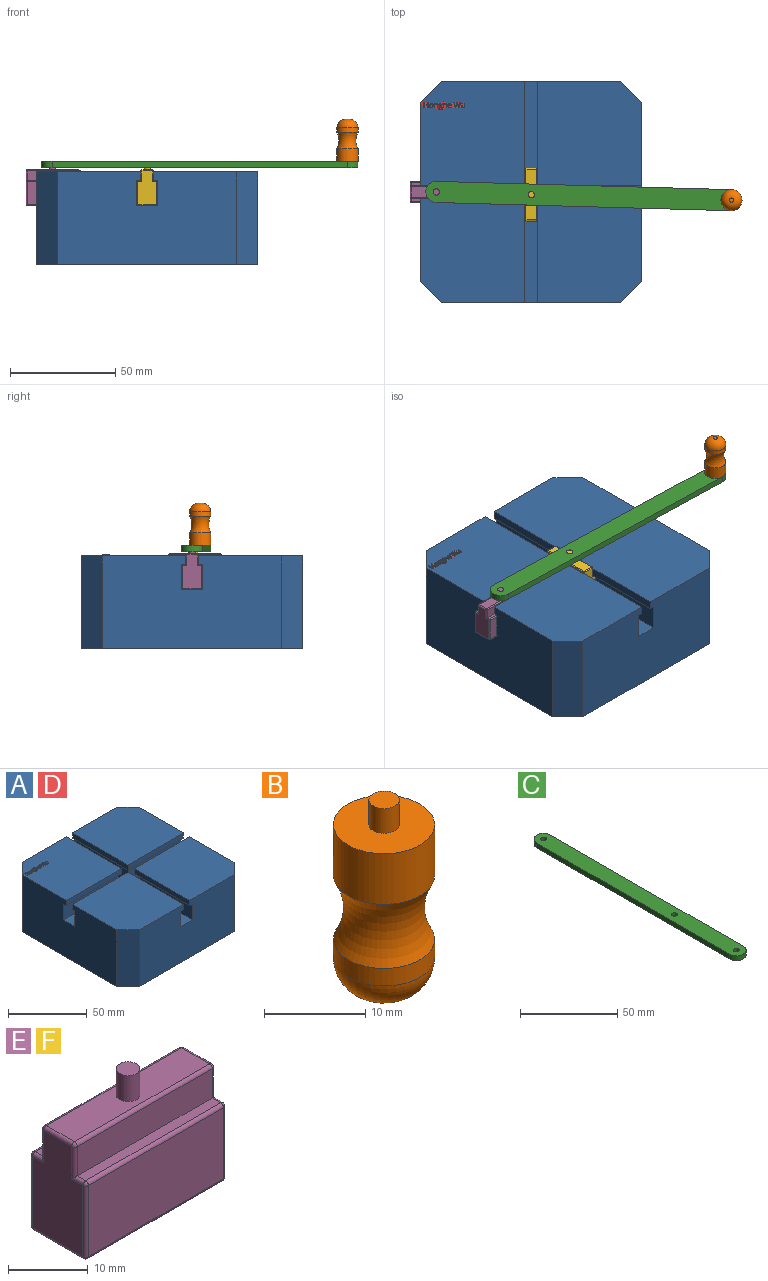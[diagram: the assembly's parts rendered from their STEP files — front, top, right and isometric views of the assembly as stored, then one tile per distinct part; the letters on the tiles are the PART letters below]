
ASSEMBLY  parts=6 mates=5
PART A: 210 faces, bbox 105x105x44.5 mm
  f0: plane 49.5x49.5mm, normal (0,0,1), area 2382.3mm2, adj f10,f15,f16,f19,f33,f34,f35,f36
  f1: plane 49.5x49.5mm, normal (0,0,1), area 2400.2mm2, adj f10,f11,f12,f25,f28
  f2: plane 49.5x49.5mm, normal (0,0,-1), area 194mm2, adj f10,f15,f19,f21,f31,f33
  f3: plane 49.5x49.5mm, normal (0,0,-1), area 194mm2, adj f10,f12,f23,f25,f27,f28
  f4: plane 49.5x4mm, normal (0,-1,0), area 198mm2, adj f9,f17,f20,f32
  f5: plane 47.5x12mm, normal (0,-1,0), area 570mm2, adj f9,f20,f22,f30
  f6: plane 47.5x12mm, normal (0,1,0), area 570mm2, adj f9,f22,f24,f29
  f7: plane 49.5x4mm, normal (0,1,0), area 198mm2, adj f8,f9,f24,f26
  f8: plane 49.5x49.5mm, normal (0,0,1), area 2400.2mm2, adj f7,f9,f12,f13,f26
  f9: plane 85x44mm, normal (1,0,0), area 3596mm2, adj f4,f5,f6,f7,f8,f13,f14,f17
  f10: plane 85x44mm, normal (-1,0,0), area 3596mm2, adj f0,f1,f2,f3,f11,f16,f18,f19
  f11: plane 44x10mm, normal (-0.71,-0.71,0), area 622.3mm2, adj f1,f10,f12,f18
  f12: plane 85x44mm, normal (0,-1,0), area 3596mm2, adj f1,f3,f8,f11,f13,f18,f22,f24
  f13: plane 44x10mm, normal (0.71,-0.71,0), area 622.3mm2, adj f8,f9,f12,f18
  f14: plane 44x10mm, normal (0.71,0.71,0), area 622.3mm2, adj f9,f15,f17,f18
  f15: plane 85x44mm, normal (0,1,0), area 3596mm2, adj f0,f2,f14,f16,f17,f18,f20,f22
  f16: plane 44x10mm, normal (-0.71,0.71,0), area 622.3mm2, adj f0,f10,f15,f18
  f17: plane 49.5x49.5mm, normal (0,0,1), area 2400.2mm2, adj f4,f9,f14,f15,f32
  f18: plane 105x105mm, normal (0,0,-1), area 10825mm2, adj f9,f10,f11,f12,f13,f14,f15,f16
  f19: plane 49.5x4mm, normal (0,-1,0), area 198mm2, adj f0,f2,f10,f33
  f20: plane 49.5x49.5mm, normal (0,0,-1), area 194mm2, adj f4,f5,f9,f15,f30,f32
  f21: plane 47.5x12mm, normal (0,-1,0), area 570mm2, adj f2,f10,f22,f31
  f22: plane 105x105mm, normal (0,0,1), area 2000mm2, adj f5,f6,f9,f10,f12,f15,f21,f23
  f23: plane 47.5x12mm, normal (0,1,0), area 570mm2, adj f3,f10,f22,f27
  f24: plane 49.5x49.5mm, normal (0,0,-1), area 194mm2, adj f6,f7,f9,f12,f26,f29
  f25: plane 49.5x4mm, normal (0,1,0), area 198mm2, adj f1,f3,f10,f28
  f26: plane 49.5x4mm, normal (-1,0,0), area 198mm2, adj f7,f8,f12,f24
  f27: plane 47.5x12mm, normal (1,0,0), area 570mm2, adj f3,f12,f22,f23
  f28: plane 49.5x4mm, normal (1,0,0), area 198mm2, adj f1,f3,f12,f25
  f29: plane 47.5x12mm, normal (-1,0,0), area 570mm2, adj f6,f12,f22,f24
  f30: plane 47.5x12mm, normal (-1,0,0), area 570mm2, adj f5,f15,f20,f22
  f31: plane 47.5x12mm, normal (1,0,0), area 570mm2, adj f2,f15,f21,f22
  f32: plane 49.5x4mm, normal (-1,0,0), area 198mm2, adj f4,f15,f17,f20
  f33: plane 49.5x4mm, normal (1,0,0), area 198mm2, adj f0,f2,f15,f19
  f34: plane 0.5x0.3mm, normal (0,-1,0), area 0.2mm2, adj f0,f35,f45,f46
  f35: plane 2.62x0.5mm, normal (1,0,0), area 1.3mm2, adj f0,f34,f36,f46
  f36: plane 0.5x0.3mm, normal (0,1,0), area 0.2mm2, adj f0,f35,f37,f46
  f37: plane 1.11x0.5mm, normal (-1,0,0), area 0.6mm2, adj f0,f36,f38,f46
  f38: plane 1.38x0.5mm, normal (0,1,0), area 0.7mm2, adj f0,f37,f39,f46
  f39: plane 1.11x0.5mm, normal (1,0,0), area 0.6mm2, adj f0,f38,f40,f46
  f40: plane 0.5x0.3mm, normal (0,1,0), area 0.2mm2, adj f0,f39,f41,f46
  f41: plane 2.62x0.5mm, normal (-1,0,0), area 1.3mm2, adj f0,f40,f42,f46
  f42: plane 0.5x0.3mm, normal (0,-1,0), area 0.2mm2, adj f0,f41,f43,f46
  f43: plane 1.23x0.5mm, normal (1,0,0), area 0.6mm2, adj f0,f42,f44,f46
  f44: plane 1.38x0.5mm, normal (0,-1,0), area 0.7mm2, adj f0,f43,f45,f46
  f45: plane 1.23x0.5mm, normal (-1,0,0), area 0.6mm2, adj f0,f34,f44,f46
  f46: plane 2.62x1.99mm, normal (0,0,1), area 2mm2, adj f34,f35,f36,f37,f38,f39,f40,f41
  f47: extruded ~0.57x0.5mm, area 0.3mm2, adj f48,f63,f64,f65
  f48: extruded ~0.57x0.5mm, area 0.3mm2, adj f47,f49,f64,f65
  f49: extruded ~0.5x0.44mm, area 0.2mm2, adj f48,f50,f64,f65
  f50: extruded ~0.5x0.45mm, area 0.3mm2, adj f49,f51,f64,f65
  f51: extruded ~0.57x0.5mm, area 0.3mm2, adj f50,f52,f64,f65
  f52: extruded ~0.57x0.5mm, area 0.3mm2, adj f51,f53,f64,f65
  f53: extruded ~0.5x0.44mm, area 0.3mm2, adj f52,f63,f64,f65
  f54: extruded ~0.75x0.5mm, area 0.4mm2, adj f0,f55,f62,f64
  f55: extruded ~0.74x0.5mm, area 0.4mm2, adj f0,f54,f56,f64
  f56: extruded ~0.65x0.5mm, area 0.4mm2, adj f0,f55,f57,f64
  f57: extruded ~0.67x0.5mm, area 0.4mm2, adj f0,f56,f58,f64
  f58: extruded ~0.75x0.5mm, area 0.4mm2, adj f0,f57,f59,f64
  f59: extruded ~0.54x0.5mm, area 0.3mm2, adj f0,f58,f60,f64
  f60: extruded ~0.5x0.35mm, area 0.2mm2, adj f0,f59,f61,f64
  f61: extruded ~0.5x0.47mm, area 0.2mm2, adj f0,f60,f62,f64
  f62: extruded ~0.67x0.5mm, area 0.4mm2, adj f0,f54,f61,f64
  f63: extruded ~0.5x0.44mm, area 0.3mm2, adj f47,f53,f64,f65
  f64: plane 2.03x1.8mm, normal (0,0,1), area 1.5mm2, adj f47,f48,f49,f50,f51,f52,f53,f54
  f65: plane 1.53x1.19mm, normal (0,0,1), area 1.5mm2, adj f47,f48,f49,f50,f51,f52,f53,f63
  f66: plane 1.27x0.5mm, normal (-1,0,0), area 0.6mm2, adj f0,f67,f82,f83
  f67: plane 0.5x0.3mm, normal (0,-1,0), area 0.1mm2, adj f0,f66,f68,f83
  f68: plane 1.28x0.5mm, normal (1,0,0), area 0.6mm2, adj f0,f67,f69,f83
  f69: extruded ~0.55x0.5mm, area 0.3mm2, adj f0,f68,f70,f83
  f70: extruded ~0.53x0.5mm, area 0.3mm2, adj f0,f69,f71,f83
  f71: extruded ~0.5x0.37mm, area 0.2mm2, adj f0,f70,f72,f83
  f72: extruded ~0.5x0.26mm, area 0.2mm2, adj f0,f71,f73,f83
  f73: plane 0.5x0.01mm, normal (0,1,0), area 0mm2, adj f0,f72,f74,f83
  f74: plane 0.5x0.27mm, normal (0.98,0.18,0), area 0.1mm2, adj f0,f73,f75,f83
  f75: plane 0.5x0.24mm, normal (0,1,0), area 0.1mm2, adj f0,f74,f76,f83
  f76: plane 1.96x0.5mm, normal (-1,0,0), area 1mm2, adj f0,f75,f77,f83
  f77: plane 0.5x0.3mm, normal (0,-1,0), area 0.1mm2, adj f0,f76,f78,f83
  f78: plane 1.03x0.5mm, normal (1,0,0), area 0.5mm2, adj f0,f77,f79,f83
  f79: extruded ~0.55x0.5mm, area 0.3mm2, adj f0,f78,f80,f83
  f80: extruded ~0.5x0.45mm, area 0.2mm2, adj f0,f79,f81,f83
  f81: extruded ~0.5x0.34mm, area 0.2mm2, adj f0,f80,f82,f83
  f82: extruded ~0.5x0.36mm, area 0.2mm2, adj f0,f66,f81,f83
  f83: plane 2x1.64mm, normal (0,0,1), area 1.4mm2, adj f66,f67,f68,f69,f70,f71,f72,f73
  f84: extruded ~0.5x0.31mm, area 0.2mm2, adj f85,f127,f128,f129
  f85: extruded ~0.5x0.33mm, area 0.2mm2, adj f84,f86,f128,f129
  f86: extruded ~0.5x0.32mm, area 0.2mm2, adj f85,f87,f128,f129
  f87: extruded ~0.5x0.44mm, area 0.4mm2, adj f86,f88,f128,f129
  f88: extruded ~0.5x0.43mm, area 0.3mm2, adj f87,f127,f128,f129
  f89: extruded ~0.5x0.24mm, area 0.1mm2, adj f90,f125,f128,f130
  f90: extruded ~0.5x0.28mm, area 0.2mm2, adj f89,f91,f128,f130
  f91: extruded ~0.5x0.32mm, area 0.2mm2, adj f90,f92,f128,f130
  f92: plane 0.5x0.36mm, normal (0,-1,0), area 0.2mm2, adj f91,f93,f128,f130
  f93: extruded ~0.5x0.37mm, area 0.2mm2, adj f92,f94,f128,f130
  f94: extruded ~0.5x0.22mm, area 0.1mm2, adj f93,f95,f128,f130
  f95: extruded ~0.5x0.3mm, area 0.2mm2, adj f94,f96,f128,f130
  f96: extruded ~0.55x0.5mm, area 0.3mm2, adj f95,f125,f128,f130
  f97: plane 0.5x0.19mm, normal (1,0,0), area 0.1mm2, adj f0,f98,f126,f128
  f98: plane 0.68x0.5mm, normal (0,1,0), area 0.3mm2, adj f0,f97,f99,f128
  f99: extruded ~0.5x0.28mm, area 0.1mm2, adj f0,f98,f100,f128
  f100: extruded ~0.55x0.5mm, area 0.3mm2, adj f0,f99,f101,f128
  f101: extruded ~0.5x0.5mm, area 0.3mm2, adj f0,f100,f102,f128
  f102: extruded ~0.5x0.34mm, area 0.2mm2, adj f0,f101,f103,f128
  f103: extruded ~0.5x0.25mm, area 0.2mm2, adj f0,f102,f104,f128
  f104: extruded ~0.5x0.18mm, area 0.1mm2, adj f0,f103,f105,f128
  f105: extruded ~0.5x0.19mm, area 0.1mm2, adj f0,f104,f106,f128
  f106: extruded ~0.5x0.17mm, area 0.1mm2, adj f0,f105,f107,f128
  f107: extruded ~0.5x0.13mm, area 0.1mm2, adj f0,f106,f108,f128
  f108: extruded ~0.5x0.32mm, area 0.2mm2, adj f0,f107,f109,f128
  f109: extruded ~0.5x0.31mm, area 0.2mm2, adj f0,f108,f110,f128
  f110: extruded ~0.5x0.41mm, area 0.2mm2, adj f0,f109,f111,f128
  f111: extruded ~0.59x0.5mm, area 0.3mm2, adj f0,f110,f112,f128
  f112: extruded ~0.76x0.5mm, area 0.4mm2, adj f0,f111,f113,f128
  f113: extruded ~0.5x0.5mm, area 0.3mm2, adj f0,f112,f114,f128
  f114: extruded ~0.5x0.39mm, area 0.2mm2, adj f0,f113,f115,f128
  f115: extruded ~0.5x0.49mm, area 0.3mm2, adj f0,f114,f116,f128
  f116: plane 0.5x0.35mm, normal (0,1,0), area 0.2mm2, adj f0,f115,f117,f128
  f117: extruded ~0.5x0.23mm, area 0.1mm2, adj f0,f116,f118,f128
  f118: extruded ~0.5x0.12mm, area 0.1mm2, adj f0,f117,f119,f128
  f119: extruded ~0.5x0.25mm, area 0.2mm2, adj f0,f118,f120,f128
  f120: extruded ~0.5x0.16mm, area 0.1mm2, adj f0,f119,f121,f128
  f121: extruded ~0.54x0.5mm, area 0.3mm2, adj f0,f120,f122,f128
  f122: extruded ~0.5x0.46mm, area 0.3mm2, adj f0,f121,f123,f128
  f123: extruded ~0.5x0.23mm, area 0.1mm2, adj f0,f122,f124,f128
  f124: extruded ~0.5x0.16mm, area 0.1mm2, adj f0,f123,f126,f128
  f125: extruded ~0.5x0.38mm, area 0.2mm2, adj f89,f96,f128,f130
  f126: plane 0.5x0.36mm, normal (0.12,-0.99,0), area 0.2mm2, adj f0,f97,f124,f128
  f127: extruded ~0.5x0.32mm, area 0.2mm2, adj f84,f88,f128,f129
  f128: plane 2.88x1.85mm, normal (0,0,1), area 2.2mm2, adj f84,f85,f86,f87,f88,f89,f90,f91
  f129: plane 0.88x0.86mm, normal (0,0,1), area 0.6mm2, adj f84,f85,f86,f87,f88,f127
  f130: plane 1.25x0.7mm, normal (0,0,1), area 0.7mm2, adj f89,f90,f91,f92,f93,f94,f95,f96
  f131: plane 1.27x0.5mm, normal (-1,0,0), area 0.6mm2, adj f0,f132,f148,f149
  f132: plane 0.5x0.3mm, normal (0,-1,0), area 0.1mm2, adj f0,f131,f133,f149
  f133: plane 1.28x0.5mm, normal (1,0,0), area 0.6mm2, adj f0,f132,f134,f149
  f134: extruded ~0.54x0.5mm, area 0.3mm2, adj f0,f133,f135,f149
  f135: extruded ~0.54x0.5mm, area 0.3mm2, adj f0,f134,f136,f149
  f136: extruded ~0.5x0.37mm, area 0.2mm2, adj f0,f135,f137,f149
  f137: extruded ~0.5x0.25mm, area 0.2mm2, adj f0,f136,f138,f149
  f138: plane 0.5x0.02mm, normal (0,1,0), area 0mm2, adj f0,f137,f139,f149
  f139: extruded ~0.5x0.25mm, area 0.1mm2, adj f0,f138,f140,f149
  f140: plane 0.84x0.5mm, normal (1,0,0), area 0.4mm2, adj f0,f139,f141,f149
  f141: plane 0.5x0.3mm, normal (0,1,0), area 0.1mm2, adj f0,f140,f142,f149
  f142: plane 2.79x0.5mm, normal (-1,0,0), area 1.4mm2, adj f0,f141,f143,f149
  f143: plane 0.5x0.3mm, normal (0,-1,0), area 0.1mm2, adj f0,f142,f144,f149
  f144: plane 1.03x0.5mm, normal (1,0,0), area 0.5mm2, adj f0,f143,f145,f149
  f145: extruded ~0.55x0.5mm, area 0.3mm2, adj f0,f144,f146,f149
  f146: extruded ~0.5x0.45mm, area 0.2mm2, adj f0,f145,f147,f149
  f147: extruded ~0.5x0.34mm, area 0.2mm2, adj f0,f146,f148,f149
  f148: extruded ~0.5x0.36mm, area 0.2mm2, adj f0,f131,f147,f149
  f149: plane 2.79x1.64mm, normal (0,0,1), area 1.6mm2, adj f131,f132,f133,f134,f135,f136,f137,f138
  f150: extruded ~0.5x0.38mm, area 0.2mm2, adj f151,f168,f169,f170
  f151: extruded ~0.5x0.36mm, area 0.2mm2, adj f150,f152,f169,f170
  f152: extruded ~0.5x0.43mm, area 0.2mm2, adj f151,f153,f169,f170
  f153: plane 1.03x0.5mm, normal (0,1,0), area 0.5mm2, adj f152,f168,f169,f170
  f154: extruded ~0.69x0.5mm, area 0.4mm2, adj f0,f155,f167,f169
  f155: extruded ~0.5x0.34mm, area 0.2mm2, adj f0,f154,f156,f169
  f156: extruded ~0.5x0.3mm, area 0.2mm2, adj f0,f155,f157,f169
  f157: plane 0.5x0.27mm, normal (1,0,0), area 0.1mm2, adj f0,f156,f158,f169
  f158: extruded ~0.63x0.5mm, area 0.3mm2, adj f0,f157,f159,f169
  f159: extruded ~0.5x0.47mm, area 0.3mm2, adj f0,f158,f160,f169
  f160: extruded ~0.52x0.5mm, area 0.3mm2, adj f0,f159,f161,f169
  f161: plane 1.35x0.5mm, normal (0,-1,0), area 0.7mm2, adj f0,f160,f162,f169
  f162: plane 0.5x0.19mm, normal (1,0,0), area 0.1mm2, adj f0,f161,f163,f169
  f163: extruded ~0.64x0.5mm, area 0.3mm2, adj f0,f162,f164,f169
  f164: extruded ~0.58x0.5mm, area 0.3mm2, adj f0,f163,f165,f169
  f165: extruded ~0.63x0.5mm, area 0.4mm2, adj f0,f164,f166,f169
  f166: extruded ~0.75x0.5mm, area 0.4mm2, adj f0,f165,f167,f169
  f167: extruded ~0.74x0.5mm, area 0.4mm2, adj f0,f154,f166,f169
  f168: extruded ~0.5x0.43mm, area 0.2mm2, adj f150,f153,f169,f170
  f169: plane 2.03x1.66mm, normal (0,0,1), area 1.5mm2, adj f150,f151,f152,f153,f154,f155,f156,f157
  f170: plane 1.03x0.58mm, normal (0,0,1), area 0.5mm2, adj f150,f151,f152,f153,f168
  f171: plane 0.5x0.3mm, normal (0,-1,0), area 0.2mm2, adj f0,f172,f190,f191
  f172: plane 2.62x0.7mm, normal (0.97,-0.26,0), area 1.4mm2, adj f0,f171,f173,f191
  f173: plane 0.5x0.32mm, normal (0,1,0), area 0.2mm2, adj f0,f172,f174,f191
  f174: plane 1.61x0.5mm, normal (-0.97,0.25,0), area 0.8mm2, adj f0,f173,f175,f191
  f175: extruded ~0.62x0.5mm, area 0.3mm2, adj f0,f174,f176,f191
  f176: extruded ~0.63x0.5mm, area 0.3mm2, adj f0,f175,f177,f191
  f177: plane 1.61x0.5mm, normal (0.96,0.29,0), area 0.8mm2, adj f0,f176,f178,f191
  f178: plane 0.5x0.32mm, normal (0,1,0), area 0.2mm2, adj f0,f177,f179,f191
  f179: plane 1.59x0.5mm, normal (-0.96,0.28,0), area 0.8mm2, adj f0,f178,f180,f191
  f180: extruded ~0.64x0.5mm, area 0.3mm2, adj f0,f179,f181,f191
  f181: extruded ~0.62x0.5mm, area 0.3mm2, adj f0,f180,f182,f191
  f182: plane 1.62x0.5mm, normal (0.97,0.25,0), area 0.8mm2, adj f0,f181,f183,f191
  f183: plane 0.5x0.32mm, normal (0,1,0), area 0.2mm2, adj f0,f182,f184,f191
  f184: plane 2.62x0.7mm, normal (-0.97,-0.26,0), area 1.4mm2, adj f0,f183,f185,f191
  f185: plane 0.5x0.3mm, normal (0,-1,0), area 0.2mm2, adj f0,f184,f186,f191
  f186: plane 1.74x0.51mm, normal (0.96,-0.28,0), area 0.9mm2, adj f0,f185,f187,f191
  f187: extruded ~0.52x0.5mm, area 0.3mm2, adj f0,f186,f188,f191
  f188: extruded ~0.5x0.21mm, area 0.1mm2, adj f0,f187,f189,f191
  f189: extruded ~0.5x0.29mm, area 0.2mm2, adj f0,f188,f190,f191
  f190: plane 1.75x0.53mm, normal (-0.96,-0.29,0), area 0.9mm2, adj f0,f171,f189,f191
  f191: plane 3.3x2.62mm, normal (0,0,1), area 2.9mm2, adj f171,f172,f173,f174,f175,f176,f177,f178
  f192: plane 1.27x0.5mm, normal (1,0,0), area 0.6mm2, adj f0,f193,f208,f209
  f193: plane 0.5x0.3mm, normal (0,1,0), area 0.2mm2, adj f0,f192,f194,f209
  f194: plane 1.28x0.5mm, normal (-1,0,0), area 0.6mm2, adj f0,f193,f195,f209
  f195: extruded ~0.54x0.5mm, area 0.3mm2, adj f0,f194,f196,f209
  f196: extruded ~0.54x0.5mm, area 0.3mm2, adj f0,f195,f197,f209
  f197: extruded ~0.5x0.37mm, area 0.2mm2, adj f0,f196,f198,f209
  f198: extruded ~0.5x0.25mm, area 0.2mm2, adj f0,f197,f199,f209
  f199: plane 0.5x0.02mm, normal (0,-1,0), area 0mm2, adj f0,f198,f200,f209
  f200: plane 0.5x0.26mm, normal (-0.99,-0.16,0), area 0.1mm2, adj f0,f199,f201,f209
  f201: plane 0.5x0.25mm, normal (0,-1,0), area 0.1mm2, adj f0,f200,f202,f209
  f202: plane 1.96x0.5mm, normal (1,0,0), area 1mm2, adj f0,f201,f203,f209
  f203: plane 0.5x0.3mm, normal (0,1,0), area 0.1mm2, adj f0,f202,f204,f209
  f204: plane 1.03x0.5mm, normal (-1,0,0), area 0.5mm2, adj f0,f203,f205,f209
  f205: extruded ~0.55x0.5mm, area 0.3mm2, adj f0,f204,f206,f209
  f206: extruded ~0.5x0.45mm, area 0.2mm2, adj f0,f205,f207,f209
  f207: extruded ~0.5x0.34mm, area 0.2mm2, adj f0,f206,f208,f209
  f208: extruded ~0.5x0.36mm, area 0.2mm2, adj f0,f192,f207,f209
  f209: plane 2x1.64mm, normal (0,0,1), area 1.4mm2, adj f192,f193,f194,f195,f196,f197,f198,f199
PART B: 8 faces, bbox 13.7x13.7x23 mm
  f0: plane 2x2mm, normal (0,0,-1), area 3.1mm2, adj f1
  f1: torus R=1mm, axis (0,0,-1), area 140mm2, adj f0,f2
  f2: cylinder r=5mm len=10mm, axis (0,0,-1), area 66.8mm2, adj f1,f3
  f3: torus R=12mm, axis (0,0,-1), area 220.3mm2, adj f2,f4
  f4: cylinder r=5mm len=10mm, axis (0,0,-1), area 192.5mm2, adj f3,f5
  f5: plane 10x10mm, normal (0,0,1), area 71.5mm2, adj f4,f6
  f6: cylinder r=1.5mm len=3mm, axis (0,0,-1), area 28.3mm2, adj f5,f7
  f7: plane 3x3mm, normal (0,0,1), area 7.1mm2, adj f6
PART C: 9 faces, bbox 10x150x3 mm
  f0: cylinder r=5mm len=10mm, axis (0,0,-1), area 47.1mm2, adj f1,f6,f7,f8
  f1: plane 140x3mm, normal (-1,0,0), area 420mm2, adj f0,f2,f7,f8
  f2: cylinder r=5mm len=10mm, axis (0,0,-1), area 47.1mm2, adj f1,f6,f7,f8
  f3: cylinder r=1.5mm len=3mm, axis (0,0,-1), area 28.3mm2, adj f7,f8
  f4: cylinder r=1.5mm len=3mm, axis (0,0,-1), area 28.3mm2, adj f7,f8
  f5: cylinder r=1.5mm len=3mm, axis (0,0,-1), area 28.3mm2, adj f7,f8
  f6: plane 140x3mm, normal (1,0,0), area 420mm2, adj f0,f2,f7,f8
  f7: plane 150x10mm, normal (0,0,1), area 1457.3mm2, adj f0,f1,f2,f3,f4,f5,f6
  f8: plane 150x10mm, normal (0,0,-1), area 1457.3mm2, adj f0,f1,f2,f3,f4,f5,f6
PART D: same geometry as A
PART E: 46 faces, bbox 25x10x21 mm
  f0: plane 24x8.95mm, normal (0,0,-1), area 214.8mm2, adj f34,f39,f42,f45
  f1: plane 24x10.95mm, normal (0,-1,0), area 262.8mm2, adj f31,f40,f41,f45
  f2: plane 24x1.5mm, normal (0,0,1), area 36mm2, adj f3,f30,f31,f32
  f3: plane 24x4.5mm, normal (0,-1,0), area 108mm2, adj f2,f17,f26,f27
  f4: plane 24x4.95mm, normal (0,0,1), area 111.7mm2, adj f10,f12,f16,f17,f18
  f5: plane 24x4.5mm, normal (0,1,0), area 108mm2, adj f6,f12,f15,f19
  f6: plane 24x1.5mm, normal (0,0,1), area 36mm2, adj f5,f20,f23,f24
  f7: plane 24x10.95mm, normal (0,1,0), area 262.8mm2, adj f24,f29,f33,f34
  f8: plane 15.95x8.95mm, normal (-1,0,0), area 122.8mm2, adj f15,f16,f20,f26,f29,f30,f39,f40
  f9: plane 15.95x8.95mm, normal (1,0,0), area 122.8mm2, adj f18,f19,f23,f27,f32,f33,f41,f42
  f10: cylinder r=1.5mm len=4mm, axis (0,0,-1), area 37.7mm2, adj f4,f11
  f11: plane 3x3mm, normal (0,0,1), area 7.1mm2, adj f10
  f12: cylinder r=0.5mm len=24mm, axis (1,0,0), area 18.8mm2, adj f4,f5,f13,f14
  f13: sphere r=0.5mm, area 0.4mm2, adj f12,f15,f16
  f14: sphere r=0.5mm, area 0.4mm2, adj f12,f18,f19
  f15: cylinder r=0.5mm len=5mm, axis (0,0,1), area 3.7mm2, adj f5,f8,f13,f20
  f16: cylinder r=0.5mm len=4.95mm, axis (0,-1,0), area 3.9mm2, adj f4,f8,f13,f21
  f17: cylinder r=0.5mm len=24mm, axis (1,0,0), area 18.8mm2, adj f3,f4,f21,f22
  f18: cylinder r=0.5mm len=4.95mm, axis (0,1,0), area 3.9mm2, adj f4,f9,f14,f22
  f19: cylinder r=0.5mm len=5mm, axis (0,0,-1), area 3.7mm2, adj f5,f9,f14,f23
  f20: cylinder r=0.5mm len=2mm, axis (0,-1,0), area 1.3mm2, adj f6,f8,f15,f25
  f21: sphere r=0.5mm, area 0.4mm2, adj f16,f17,f26
  f22: sphere r=0.5mm, area 0.4mm2, adj f17,f18,f27
  f23: cylinder r=0.5mm len=2mm, axis (0,1,0), area 1.3mm2, adj f6,f9,f19,f28
  f24: cylinder r=0.5mm len=24mm, axis (1,0,0), area 18.8mm2, adj f6,f7,f25,f28
  f25: sphere r=0.5mm, area 0.4mm2, adj f20,f24,f29
  f26: cylinder r=0.5mm len=5mm, axis (0,0,-1), area 3.7mm2, adj f3,f8,f21,f30
  f27: cylinder r=0.5mm len=5mm, axis (0,0,1), area 3.7mm2, adj f3,f9,f22,f32
  f28: sphere r=0.5mm, area 0.4mm2, adj f23,f24,f33
  f29: cylinder r=0.5mm len=10.95mm, axis (0,0,1), area 8.6mm2, adj f7,f8,f25,f35
  f30: cylinder r=0.5mm len=2mm, axis (0,-1,0), area 1.3mm2, adj f2,f8,f26,f36
  f31: cylinder r=0.5mm len=24mm, axis (1,0,0), area 18.8mm2, adj f1,f2,f36,f37
  f32: cylinder r=0.5mm len=2mm, axis (0,1,0), area 1.3mm2, adj f2,f9,f27,f37
  f33: cylinder r=0.5mm len=10.95mm, axis (0,0,-1), area 8.6mm2, adj f7,f9,f28,f38
  f34: cylinder r=0.5mm len=24mm, axis (1,0,0), area 18.8mm2, adj f0,f7,f35,f38
  f35: sphere r=0.5mm, area 0.4mm2, adj f29,f34,f39
  f36: sphere r=0.5mm, area 0.4mm2, adj f30,f31,f40
  f37: sphere r=0.5mm, area 0.4mm2, adj f31,f32,f41
  f38: sphere r=0.5mm, area 0.4mm2, adj f33,f34,f42
  f39: cylinder r=0.5mm len=8.95mm, axis (0,1,0), area 7mm2, adj f0,f8,f35,f43
  f40: cylinder r=0.5mm len=10.95mm, axis (0,0,-1), area 8.6mm2, adj f1,f8,f36,f43
  f41: cylinder r=0.5mm len=10.95mm, axis (0,0,1), area 8.6mm2, adj f1,f9,f37,f44
  f42: cylinder r=0.5mm len=8.95mm, axis (0,-1,0), area 7mm2, adj f0,f9,f38,f44
  f43: sphere r=0.5mm, area 0.4mm2, adj f39,f40,f45
  f44: sphere r=0.5mm, area 0.4mm2, adj f41,f42,f45
  f45: cylinder r=0.5mm len=24mm, axis (1,0,0), area 18.8mm2, adj f0,f1,f43,f44
PART F: same geometry as E
PLACE A t=(49.64,-35.17,6.47)mm fixed
PLACE B rot(axis=(1,-0.04,0),180deg) t=(-2.44,85.7,214.59)mm
PLACE C rot(axis=(0,0,-1),91.6deg) t=(-45.93,84.81,52.44)mm
PLACE D t=(49.64,-35.17,6.47)mm
PLACE E t=(69.69,59.28,28.49)mm
PLACE F rot(axis=(0,0,1),90deg) t=(-44.81,133.55,28.49)mm
MATE parallel F.f1 <-> A.f29  axis (1,0,0) through (2.14,16.05,40.47)mm
MATE parallel A.f23 <-> E.f1  axis (0,1,0) through (-55.36,12.33,40.47)mm
MATE cylindrical B.f1 <-> C.f0  axis (0,0,1) through (92.13,13.41,55.44)mm
MATE cylindrical C.f5 <-> F.f10  axis (0,0,1) through (-2.83,16.05,55.44)mm
MATE cylindrical C.f2 <-> E.f10  axis (0,0,1) through (-47.81,17.3,55.44)mm
